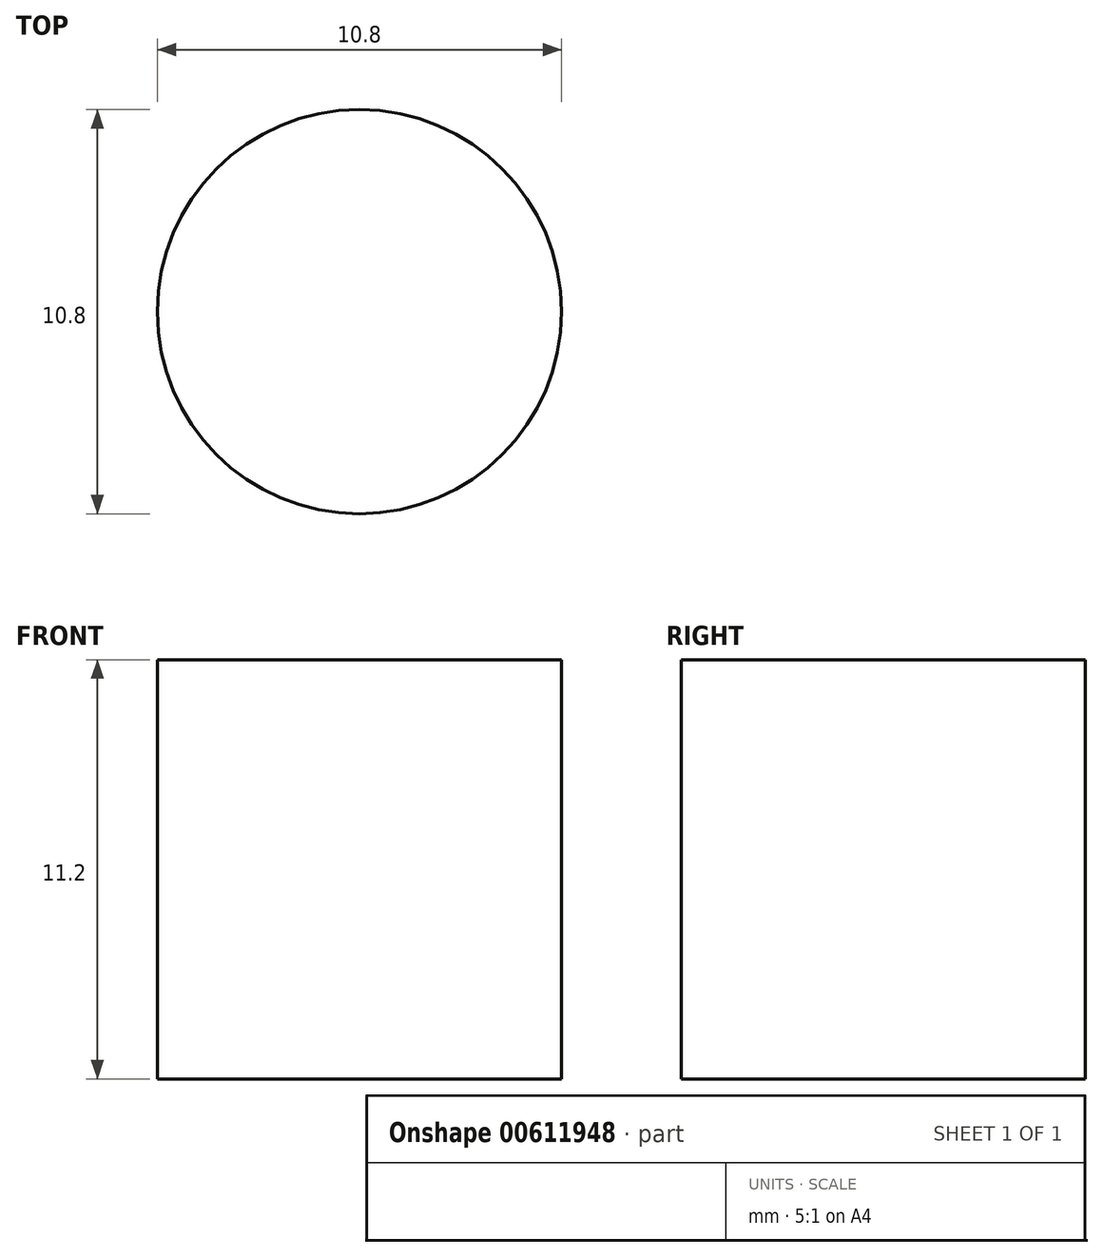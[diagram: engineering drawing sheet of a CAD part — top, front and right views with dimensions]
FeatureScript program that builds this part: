
annotation { "Feature Type Name" : "Feature", "Feature Type Description" : "" }
export const myFeature = defineFeature(function(context is Context, id is Id, definition is map)
    precondition{}
    {
        {
            var Q0;
            Q0=qCreatedBy(makeId("Top.planeOp"),FACE);
            var sketch = newSketch(context, id + "F0", { "sketchPlane" : qUnion([Q0])});
            skCircle(sketch, "E0", {"center": v(0, 0) * mm, "radius": 5.4 * mm});
            skSolve(sketch);
        }
        {
            var Q0;
            Q0 = qSketchRegion(id + "F0", true);
            extrude(context, id + "F1", {"entities" : qUnion([Q0]), "depth" : 11.2 * mm, "offsetDistance" : 25 * mm});
        }
    });
